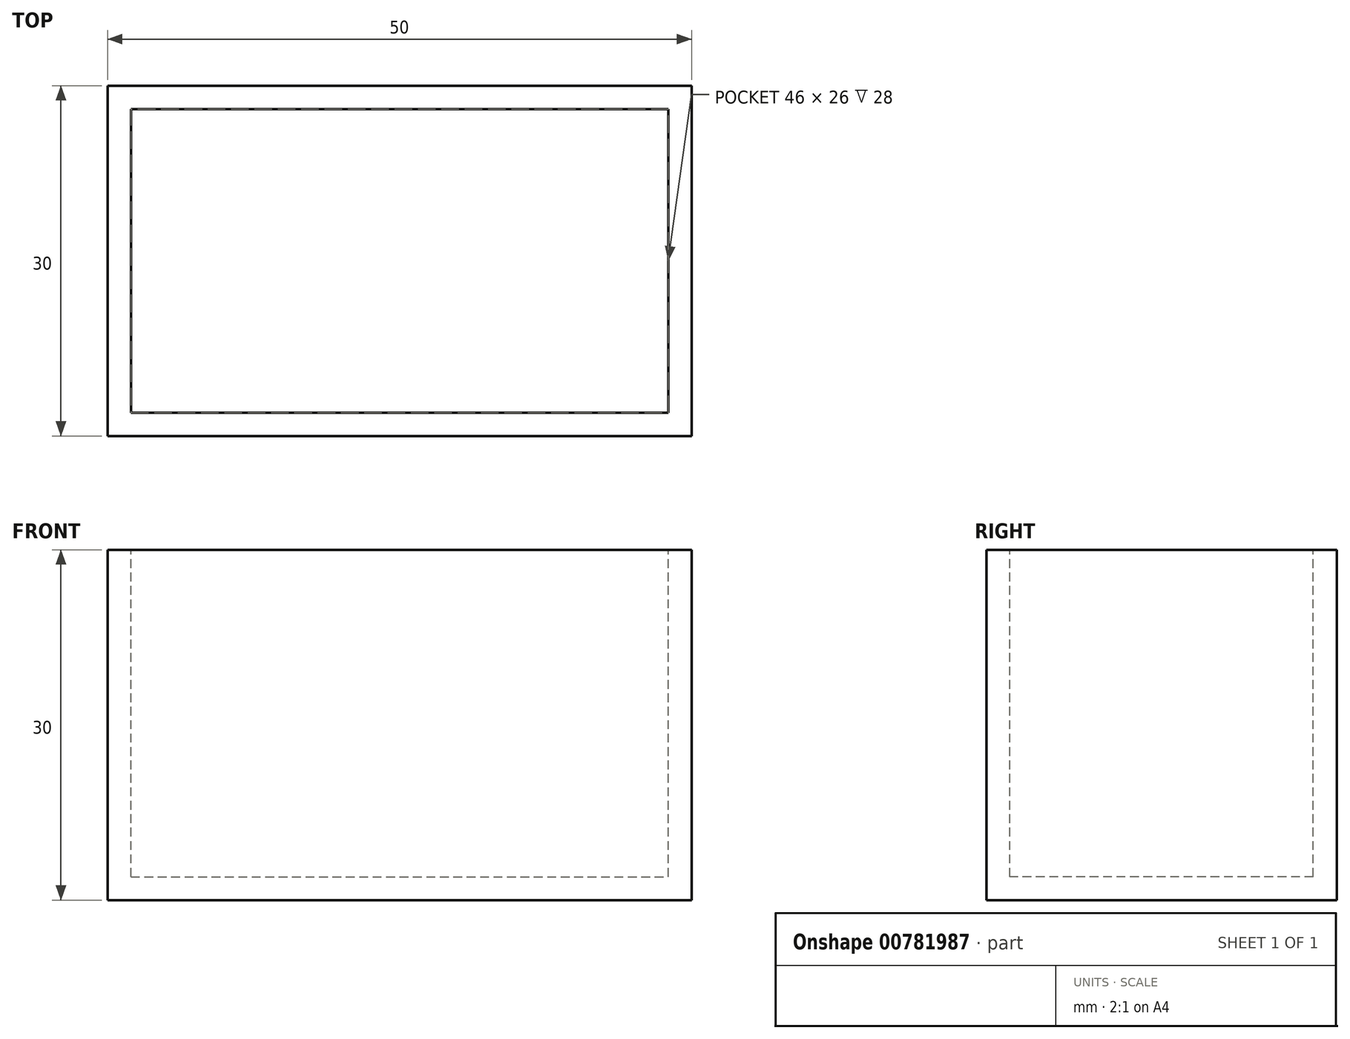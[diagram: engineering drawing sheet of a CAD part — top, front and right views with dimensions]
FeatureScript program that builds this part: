
annotation { "Feature Type Name" : "Feature", "Feature Type Description" : "" }
export const myFeature = defineFeature(function(context is Context, id is Id, definition is map)
    precondition{}
    {
        {
            var Q0;
            Q0=qCreatedBy(makeId("Top.planeOp"),FACE);
            var sketch = newSketch(context, id + "F0", { "sketchPlane" : qUnion([Q0])});
            skLineSegment(sketch, "E0.bottom", {"start": v(-50, 30) * mm, "end": v(0, 30) * mm});
            skLineSegment(sketch, "E0.top", {"start": v(-50, 0) * mm, "end": v(0, 0) * mm});
            skLineSegment(sketch, "E0.left", {"start": v(-50, 30) * mm, "end": v(-50, 0) * mm});
            skLineSegment(sketch, "E0.right", {"start": v(0, 30) * mm, "end": v(0, 0) * mm});
            skSolve(sketch);
        }
        {
            var Q0;
            Q0=makeQuery(id+"F0.imprint","IMPRINT",FACE,{"disambiguationData":[TD([[makeQuery(id+"F0.imprint","IMPRINT",EDGE,{"derivedFrom":sQuery(id+"F0.wireOp",EDGE,"E0.bottom")}),-1.0]])]});
            extrude(context, id + "F1", {"entities" : qUnion([Q0]), "depth" : 30 * mm, "offsetDistance" : 25 * mm});
        }
        {
            var Q0;
            Q0=makeQuery(id+"F1.opExtrude","CAP_FACE",FACE,{"disambiguationData":[OSD([sQuery(id+"F0.wireOp",EDGE,"E0.bottom"),sQuery(id+"F0.wireOp",EDGE,"E0.top"),sQuery(id+"F0.wireOp",EDGE,"E0.left"),sQuery(id+"F0.wireOp",EDGE,"E0.right")])],"isStart":false});
            var sketch = newSketch(context, id + "F2", { "sketchPlane" : qUnion([Q0])});
            skLineSegment(sketch, "E1", {"start": v(-50, 30) * mm, "end": v(-50, 28) * mm});
            skLineSegment(sketch, "E2", {"start": v(-50, 28) * mm, "end": v(-48, 28) * mm});
            skLineSegment(sketch, "E3.bottom", {"start": v(-48, 28) * mm, "end": v(-2, 28) * mm});
            skLineSegment(sketch, "E3.top", {"start": v(-48, 2) * mm, "end": v(-2, 2) * mm});
            skLineSegment(sketch, "E3.left", {"start": v(-48, 28) * mm, "end": v(-48, 2) * mm});
            skLineSegment(sketch, "E3.right", {"start": v(-2, 28) * mm, "end": v(-2, 2) * mm});
            skSolve(sketch);
        }
        {
            var Q0;
            Q0 = qSketchRegion(id + "F2", true);
            extrude(context, id + "F3", {"entities" : qUnion([Q0]), "operationType" : NewBodyOperationType.REMOVE, "oppositeDirection" : true, "depth" : 28 * mm, "offsetDistance" : 25 * mm});
        }
    });
